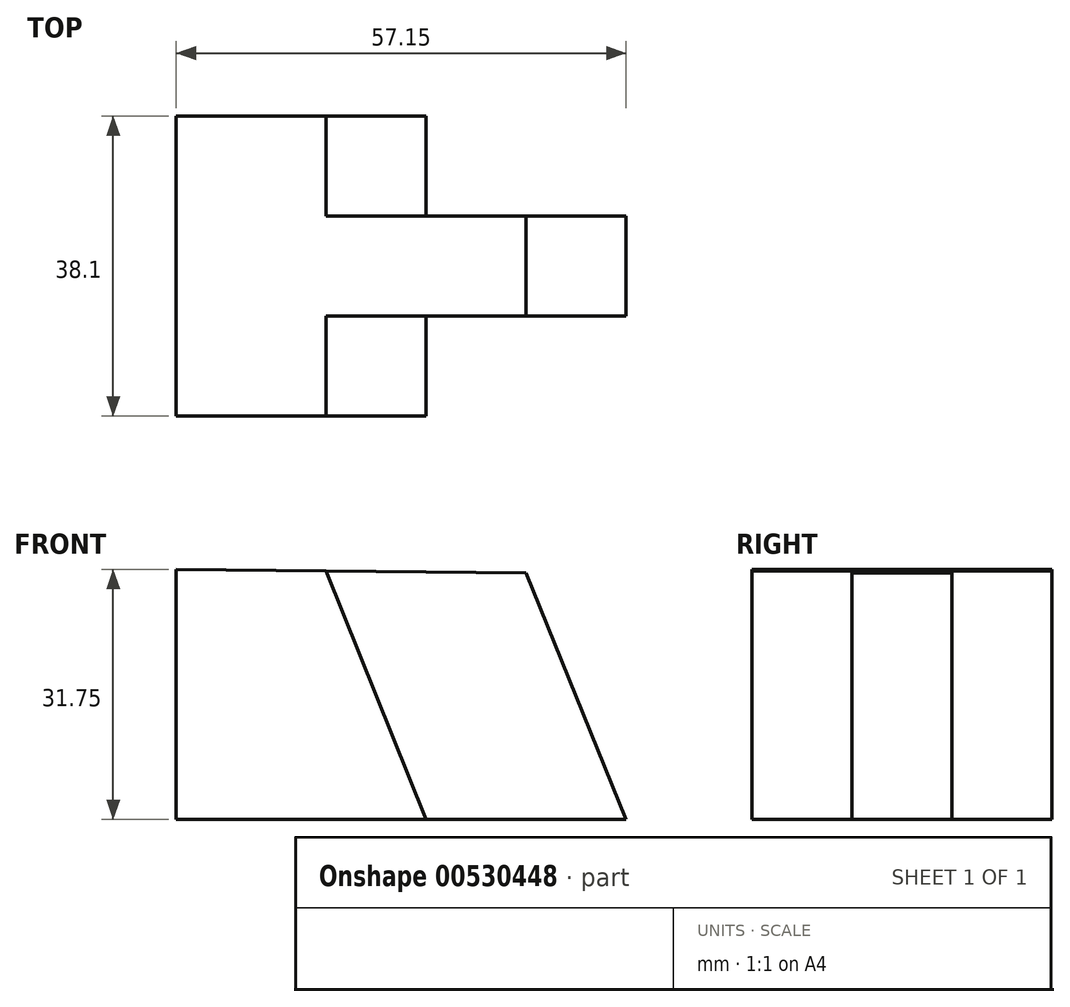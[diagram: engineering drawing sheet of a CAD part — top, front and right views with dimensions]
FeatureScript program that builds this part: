
annotation { "Feature Type Name" : "Feature", "Feature Type Description" : "" }
export const myFeature = defineFeature(function(context is Context, id is Id, definition is map)
    precondition{}
    {
        {
            var Q0;
            Q0=qCreatedBy(makeId("Front.planeOp"),FACE);
            var sketch = newSketch(context, id + "F0", { "sketchPlane" : qUnion([Q0])});
            skLineSegment(sketch, "E0", {"start": v(-44.45, 63.64) * mm, "end": v(-44.45, 31.89) * mm});
            skLineSegment(sketch, "E1", {"start": v(-44.45, 31.89) * mm, "end": v(12.7, 31.89) * mm});
            skLineSegment(sketch, "E2", {"start": v(12.7, 31.89) * mm, "end": v(0, 63.18) * mm});
            skLineSegment(sketch, "E3", {"start": v(0, 63.18) * mm, "end": v(-44.45, 63.64) * mm});
            skSolve(sketch);
        }
        {
            var Q0;
            Q0=makeQuery(id+"F0.imprint","IMPRINT",FACE,{"disambiguationData":[TD([[makeQuery(id+"F0.imprint","IMPRINT",EDGE,{"derivedFrom":sQuery(id+"F0.wireOp",EDGE,"E0")}),1.0]])]});
            extrude(context, id + "F1", {"entities" : qUnion([Q0]), "depth" : 38.1 * mm, "offsetDistance" : 25.4 * mm});
        }
        {
            var Q0;
            Q0=makeQuery(id+"F1.opExtrude","CAP_FACE",FACE,{"disambiguationData":[OSD([sQuery(id+"F0.wireOp",EDGE,"E0"),sQuery(id+"F0.wireOp",EDGE,"E1"),sQuery(id+"F0.wireOp",EDGE,"E2"),sQuery(id+"F0.wireOp",EDGE,"E3")])],"isStart":false});
            var sketch = newSketch(context, id + "F2", { "sketchPlane" : qUnion([Q0])});
            skLineSegment(sketch, "E4", {"start": v(-25.4, 63.44) * mm, "end": v(-12.7, 31.89) * mm});
            skSolve(sketch);
        }
        {
            var Q0;
            {var subQ0=sQuery(id+"F2.wireOp",EDGE,"E4");Q0=makeQuery(id+"F2.imprint","IMPRINT",FACE,{"disambiguationData":[TD([[makeQuery(id+"F2.imprint","IMPRINT",EDGE,{"derivedFrom":subQ0}),1.0]])]});}
            extrude(context, id + "F3", {"entities" : qUnion([Q0]), "operationType" : NewBodyOperationType.REMOVE, "oppositeDirection" : true, "depth" : 12.7 * mm, "offsetDistance" : 25.4 * mm});
        }
        {
            var Q0;
            Q0=makeQuery(id+"F1.opExtrude","CAP_FACE",FACE,{"disambiguationData":[OSD([sQuery(id+"F0.wireOp",EDGE,"E0"),sQuery(id+"F0.wireOp",EDGE,"E1"),sQuery(id+"F0.wireOp",EDGE,"E2"),sQuery(id+"F0.wireOp",EDGE,"E3")])],"isStart":true});
            var sketch = newSketch(context, id + "F4", { "sketchPlane" : qUnion([Q0])});
            skLineSegment(sketch, "E5", {"start": v(25.4, 63.44) * mm, "end": v(12.7, 31.89) * mm});
            skSolve(sketch);
        }
        {
            var Q0;
            {var subQ0=sQuery(id+"F4.wireOp",EDGE,"E5");Q0=makeQuery(id+"F4.imprint","IMPRINT",FACE,{"disambiguationData":[TD([[makeQuery(id+"F4.imprint","IMPRINT",EDGE,{"derivedFrom":subQ0}),-1.0]])]});}
            extrude(context, id + "F5", {"entities" : qUnion([Q0]), "operationType" : NewBodyOperationType.REMOVE, "oppositeDirection" : true, "depth" : 12.7 * mm, "offsetDistance" : 25.4 * mm});
        }
    });
